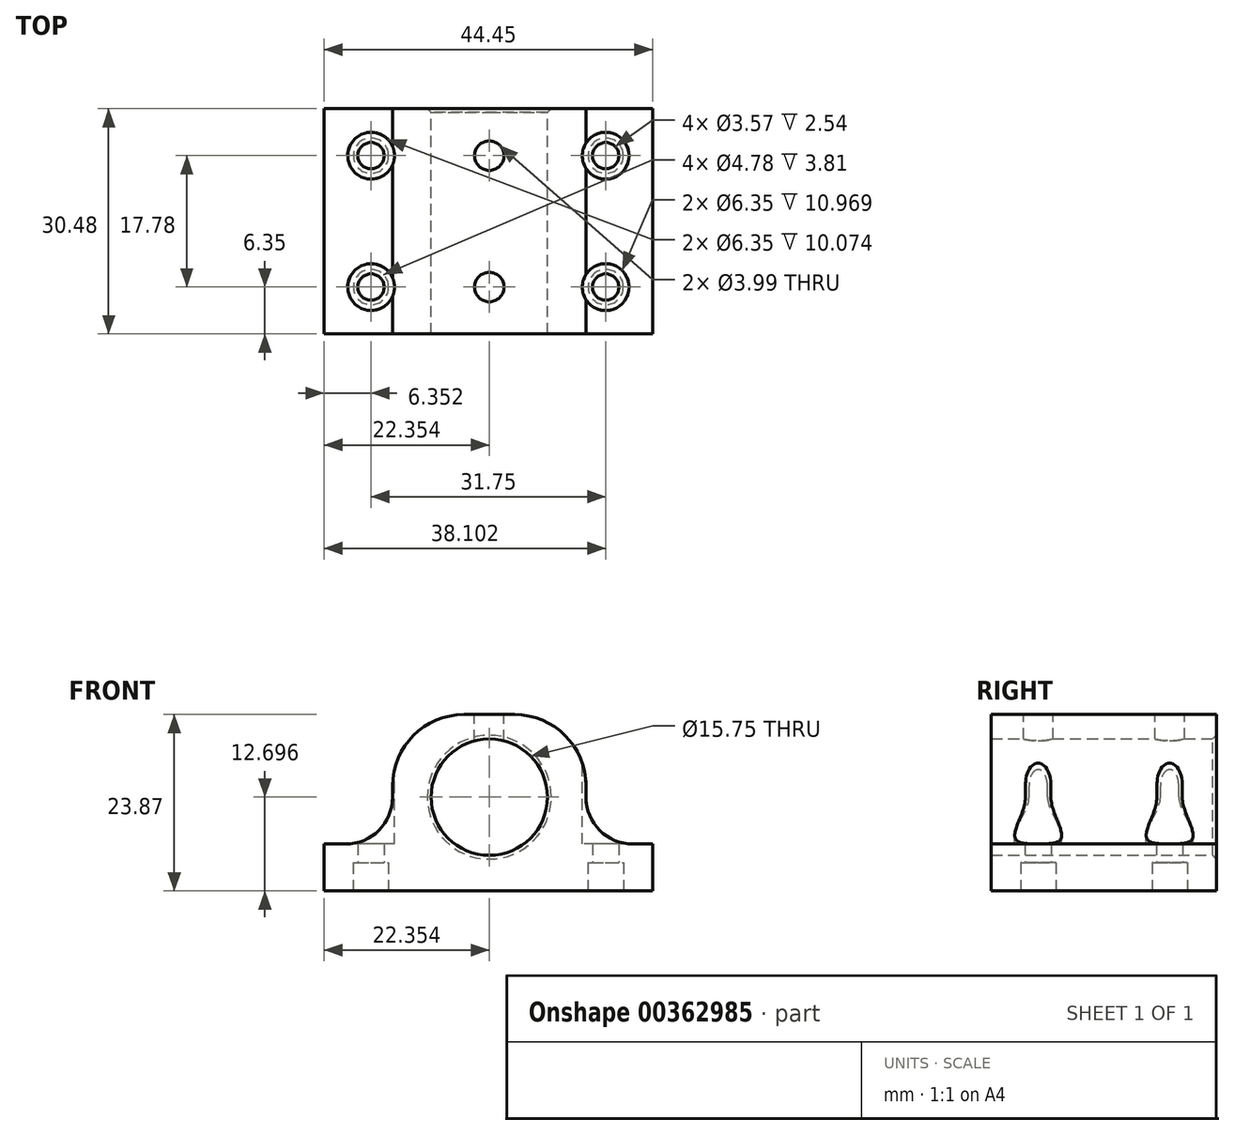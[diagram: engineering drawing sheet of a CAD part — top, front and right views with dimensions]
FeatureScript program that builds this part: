
annotation { "Feature Type Name" : "Feature", "Feature Type Description" : "" }
export const myFeature = defineFeature(function(context is Context, id is Id, definition is map)
    precondition{}
    {
        {
            var Q0;
            Q0=qCreatedBy(makeId("Front.planeOp"),FACE);
            var sketch = newSketch(context, id + "F0", { "sketchPlane" : qUnion([Q0])});
            skLineSegment(sketch, "E0", {"start": v(-40.06, 14.32) * mm, "end": v(4.4, 14.32) * mm});
            skLineSegment(sketch, "E1.0", {"start": v(-40.06, 20.67) * mm, "end": v(-37.14, 20.67) * mm});
            skLineSegment(sketch, "E2.0", {"start": v(-21.14, 38.2) * mm, "end": v(-14.28, 38.2) * mm});
            skLineSegment(sketch, "E3", {"start": v(-40.06, 20.67) * mm, "end": v(-40.06, 14.32) * mm});
            skLineSegment(sketch, "E4", {"start": v(4.4, 20.67) * mm, "end": v(4.4, 14.32) * mm});
            skCircle(sketch, "E5", {"center": v(-17.7, 27.02) * mm, "radius": 7.87 * mm});
            skLineSegment(sketch, "E6.0", {"start": v(-30.79, 28.54) * mm, "end": v(-30.79, 27.02) * mm});
            skLineSegment(sketch, "E7.0", {"start": v(-4.63, 28.54) * mm, "end": v(-4.63, 27.02) * mm});
            skLineSegment(sketch, "E8.trimOffspring", {"start": v(1.72, 20.67) * mm, "end": v(4.4, 20.67) * mm});
            skPoint(sketch, "E9.visualSharp", {"position": v(-30.79, 38.2) * mm});
            skArc(sketch, "E9.filletArc", {"start": v(-21.14, 38.2) * mm, "mid": v(-27.96, 35.37) * mm, "end": v(-30.79, 28.54) * mm});
            skPoint(sketch, "E10.visualSharp", {"position": v(-4.63, 38.2) * mm});
            skArc(sketch, "E10.filletArc", {"start": v(-4.63, 28.54) * mm, "mid": v(-7.45, 35.37) * mm, "end": v(-14.28, 38.2) * mm});
            skPoint(sketch, "E11.visualSharp", {"position": v(-30.79, 20.67) * mm});
            skArc(sketch, "E11.filletArc", {"start": v(-37.14, 20.67) * mm, "mid": v(-32.65, 22.53) * mm, "end": v(-30.79, 27.02) * mm});
            skPoint(sketch, "E12.visualSharp", {"position": v(-4.63, 20.67) * mm});
            skArc(sketch, "E12.filletArc", {"start": v(-4.63, 27.02) * mm, "mid": v(-2.77, 22.53) * mm, "end": v(1.72, 20.67) * mm});
            skSolve(sketch);
        }
        {
            var Q0;
            Q0=makeQuery(id+"F0.imprint","IMPRINT",FACE,{"disambiguationData":[TD([[makeQuery(id+"F0.imprint","IMPRINT",EDGE,{"derivedFrom":sQuery(id+"F0.wireOp",EDGE,"E0")}),1.0]])]});
            extrude(context, id + "F1", {"entities" : qUnion([Q0]), "depth" : 30.48 * mm});
        }
        {
            var Q0;
            Q0=makeQuery(id+"F1.opExtrude","SWEPT_FACE",FACE,{"disambiguationData":[OSD([sQuery(id+"F0.wireOp",EDGE,"E0")])]});
            var sketch = newSketch(context, id + "F2", { "sketchPlane" : qUnion([Q0])});
            skPoint(sketch, "E13", {"position": v(-33.7, 24.13) * mm});
            skPoint(sketch, "E14", {"position": v(-33.7, 6.35) * mm});
            skPoint(sketch, "E15", {"position": v(-1.96, 6.35) * mm});
            skPoint(sketch, "E16", {"position": v(-1.96, 24.13) * mm});
            skCircle(sketch, "E17", {"center": v(-33.7, 24.13) * mm, "radius": 2.39 * mm});
            skCircle(sketch, "E18", {"center": v(-1.96, 24.13) * mm, "radius": 2.39 * mm});
            skCircle(sketch, "E19", {"center": v(-1.96, 6.35) * mm, "radius": 2.39 * mm});
            skCircle(sketch, "E20", {"center": v(-33.7, 6.35) * mm, "radius": 2.39 * mm});
            skSolve(sketch);
        }
        {
            var Q0;
            Q0=sQuery(id+"F2.wireOp",VERTEX,"E13");
            var Q1;
            Q1=sQuery(id+"F2.wireOp",VERTEX,"E14");
            var Q2;
            Q2=sQuery(id+"F2.wireOp",VERTEX,"E16");
            var Q3;
            Q3=sQuery(id+"F2.wireOp",VERTEX,"E15");
            var Q4;
            Q4=makeQuery(id+"F1.opExtrude","SWEPT_BODY",BODY,{"disambiguationData":[OSD([sQuery(id+"F0.wireOp",EDGE,"E0"),sQuery(id+"F0.wireOp",EDGE,"E1.0"),sQuery(id+"F0.wireOp",EDGE,"E2.0"),sQuery(id+"F0.wireOp",EDGE,"E3"),sQuery(id+"F0.wireOp",EDGE,"E4"),sQuery(id+"F0.wireOp",EDGE,"E5"),sQuery(id+"F0.wireOp",EDGE,"E6.0"),sQuery(id+"F0.wireOp",EDGE,"E7.0"),sQuery(id+"F0.wireOp",EDGE,"E8.trimOffspring"),sQuery(id+"F0.wireOp",EDGE,"E9.filletArc"),sQuery(id+"F0.wireOp",EDGE,"E10.filletArc"),sQuery(id+"F0.wireOp",EDGE,"E11.filletArc"),sQuery(id+"F0.wireOp",EDGE,"E12.filletArc")])]});
            hole(context, id + "F3", {"style" : HoleStyle.SIMPLE, "endStyle" : HoleEndStyle.THROUGH, "standardTappedOrClearance" : lookupTablePath({ "standard" : "ANSI", "size" : "#28 (0.14)", "type" : "Drilled" }), "standardBlindInLast" : lookupTablePath({ "standard" : "ANSI", "size" : "#28", "type" : "Drilled" }), "holeDiameter" : 3.57 * mm, "tappedDepth" : 5.4 * mm, "tapClearance" : 3, "locations" : qUnion([Q0, Q1, Q2, Q3]), "scope" : qUnion([Q4])});
        }
        {
            var Q0;
            Q0=makeQuery(id+"F2.imprint","IMPRINT",FACE,{"disambiguationData":[TD([[makeQuery(id+"F2.imprint","IMPRINT",EDGE,{"derivedFrom":sQuery(id+"F2.wireOp",EDGE,"E17")}),1.0]])]});
            var Q1;
            Q1=makeQuery(id+"F2.imprint","IMPRINT",FACE,{"disambiguationData":[TD([[makeQuery(id+"F2.imprint","IMPRINT",EDGE,{"derivedFrom":sQuery(id+"F2.wireOp",EDGE,"E19")}),1.0]])]});
            var Q2;
            Q2=makeQuery(id+"F2.imprint","IMPRINT",FACE,{"disambiguationData":[TD([[makeQuery(id+"F2.imprint","IMPRINT",EDGE,{"derivedFrom":sQuery(id+"F2.wireOp",EDGE,"E20")}),1.0]])]});
            var Q3;
            Q3=makeQuery(id+"F2.imprint","IMPRINT",FACE,{"disambiguationData":[TD([[makeQuery(id+"F2.imprint","IMPRINT",EDGE,{"derivedFrom":sQuery(id+"F2.wireOp",EDGE,"E18")}),1.0]])]});
            extrude(context, id + "F4", {"entities" : qUnion([Q0, Q1, Q2, Q3]), "operationType" : NewBodyOperationType.REMOVE, "oppositeDirection" : true, "depth" : 3.8 * mm});
        }
        {
            var Q0;
            Q0=makeQuery(id+"F1.opExtrude","SWEPT_FACE",FACE,{"disambiguationData":[OSD([sQuery(id+"F0.wireOp",EDGE,"E1.0")])]});
            cPlane(context, id + "F5", {"entities" : qUnion([Q0]), "cplaneType" : CPlaneType.OFFSET, "offset" : 12.7 * mm, "width" : 152.4 * mm, "height" : 152.4 * mm});
        }
        {
            var Q0;
            Q0=qCreatedBy(id+"F5.planeOp",FACE);
            var sketch = newSketch(context, id + "F6", { "sketchPlane" : qUnion([Q0])});
            skPoint(sketch, "E21.0", {"position": v(-33.7, -6.35) * mm});
            skPoint(sketch, "E22.0", {"position": v(-1.96, -6.35) * mm});
            skPoint(sketch, "E23.0", {"position": v(-1.96, -24.13) * mm});
            skPoint(sketch, "E24.0", {"position": v(-33.7, -24.13) * mm});
            skCircle(sketch, "E25", {"center": v(-33.7, -6.35) * mm, "radius": 3.18 * mm});
            skCircle(sketch, "E26", {"center": v(-1.96, -6.35) * mm, "radius": 3.18 * mm});
            skCircle(sketch, "E27", {"center": v(-1.96, -24.13) * mm, "radius": 3.18 * mm});
            skCircle(sketch, "E28", {"center": v(-33.7, -24.13) * mm, "radius": 3.18 * mm});
            skSolve(sketch);
        }
        {
            var Q0;
            Q0=makeQuery(id+"F6.imprint","IMPRINT",FACE,{"disambiguationData":[TD([[makeQuery(id+"F6.imprint","IMPRINT",EDGE,{"derivedFrom":sQuery(id+"F6.wireOp",EDGE,"E25")}),1.0]])]});
            var Q1;
            Q1=makeQuery(id+"F6.imprint","IMPRINT",FACE,{"disambiguationData":[TD([[makeQuery(id+"F6.imprint","IMPRINT",EDGE,{"derivedFrom":sQuery(id+"F6.wireOp",EDGE,"E28")}),1.0]])]});
            var Q2;
            Q2=makeQuery(id+"F6.imprint","IMPRINT",FACE,{"disambiguationData":[TD([[makeQuery(id+"F6.imprint","IMPRINT",EDGE,{"derivedFrom":sQuery(id+"F6.wireOp",EDGE,"E26")}),1.0]])]});
            var Q3;
            Q3=makeQuery(id+"F6.imprint","IMPRINT",FACE,{"disambiguationData":[TD([[makeQuery(id+"F6.imprint","IMPRINT",EDGE,{"derivedFrom":sQuery(id+"F6.wireOp",EDGE,"E27")}),1.0]])]});
            extrude(context, id + "F7", {"entities" : qUnion([Q0, Q1, Q2, Q3]), "operationType" : NewBodyOperationType.REMOVE, "oppositeDirection" : true, "depth" : 12.7 * mm});
        }
        {
            var Q0;
            Q0=makeQuery(id+"F1.opExtrude","SWEPT_FACE",FACE,{"disambiguationData":[OSD([sQuery(id+"F0.wireOp",EDGE,"E2.0")])]});
            var sketch = newSketch(context, id + "F8", { "sketchPlane" : qUnion([Q0])});
            skPoint(sketch, "E29", {"position": v(-17.7, -6.35) * mm});
            skPoint(sketch, "E29.positionSnap0", {"position": v(-17.7, 0) * mm});
            skPoint(sketch, "E30", {"position": v(-17.7, -24.13) * mm});
            skSolve(sketch);
        }
        {
            var Q0;
            Q0=sQuery(id+"F8.wireOp",VERTEX,"E29");
            var Q1;
            Q1=sQuery(id+"F8.wireOp",VERTEX,"E30");
            var Q2;
            Q2=makeQuery(id+"F1.opExtrude","SWEPT_BODY",BODY,{"disambiguationData":[OSD([sQuery(id+"F0.wireOp",EDGE,"E0"),sQuery(id+"F0.wireOp",EDGE,"E1.0"),sQuery(id+"F0.wireOp",EDGE,"E2.0"),sQuery(id+"F0.wireOp",EDGE,"E3"),sQuery(id+"F0.wireOp",EDGE,"E4"),sQuery(id+"F0.wireOp",EDGE,"E5"),sQuery(id+"F0.wireOp",EDGE,"E6.0"),sQuery(id+"F0.wireOp",EDGE,"E7.0"),sQuery(id+"F0.wireOp",EDGE,"E8.trimOffspring"),sQuery(id+"F0.wireOp",EDGE,"E9.filletArc"),sQuery(id+"F0.wireOp",EDGE,"E10.filletArc"),sQuery(id+"F0.wireOp",EDGE,"E11.filletArc"),sQuery(id+"F0.wireOp",EDGE,"E12.filletArc")])]});
            hole(context, id + "F9", {"style" : HoleStyle.SIMPLE, "endStyle" : HoleEndStyle.BLIND, "standardTappedOrClearance" : lookupTablePath({ "standard" : "ANSI", "size" : "#22 (0.16)", "type" : "Drilled" }), "standardBlindInLast" : lookupTablePath({ "standard" : "ANSI", "size" : "#22", "type" : "Drilled" }), "holeDiameter" : 4 * mm, "holeDepth" : 6.35 * mm, "tappedDepth" : 5.4 * mm, "tapClearance" : 3, "locations" : qUnion([Q0, Q1]), "scope" : qUnion([Q2])});
        }
        {
            var Q0;
            Q0=makeQuery(id+"F1.opExtrude","CAP_EDGE",EDGE,{"disambiguationData":[OSD([sQuery(id+"F0.wireOp",EDGE,"E5")])],"isStart":true});
            chamfer(context, id + "F10", {"entities" : qUnion([Q0]), "chamferType" : ChamferType.OFFSET_ANGLE, "width" : 0.5 * mm, "oppositeDirection" : false, "angle" : 45 * degree, "tangentPropagation" : true});
        }
    });
